# Revit family: xFaucet-Single_Control-American_Standard-Colony_Pro-7075.10x_Series
name_source: partatom
category: Plumbing Fixtures
revit_build: Autodesk Revit 2014 (Build: 20130308_1515(x64)
units: mm (PartAtom-declared; Revit-internal decimal feet)

## types (3) — shared parameters
ADA Compliant = Yes
Assembly Code = D2020300
CW Connection = Yes
CWFU = 1.5
Cold Water Connection Diameter = 3/8"
Cold Water Connection Radius = 3/16"
Default Elevation = 0"
Flow Rate = 1.2 gmp/4.5 L/min
HW Connection = Yes
HWFU = 1.5
Height = 6 3/16"
Hot Water Connection Diameter = 0"
Hot Water Connection Radius = 3/16"
Installation Type = Fitting can be mounted on 4" centers using optional escutcheon (2000.102P) or single hole mounting method.
Length = 6 3/8"
Manufacturer = American Standard
Material = Metal-American Standard-002-Polished Chrome
Price = Prices may vary. Please consult Manufacturer Representative for most up-to-date price list.
Product URL = https://www.americanstandard-us.com
URL = http://www.americanstandard-us.com
Vent Connection = No
Warranty Information = Faucet Lifetime Function And Finish Limited Warranty.
Waste Connection = No
Width = 2"
zero-valued in all types: WFU

## per-type parameters (varying)
| type | Description | Pop-up drain handle |
| 7075.100 | Colony PRO Single Control Lavatory Faucet. Metal lever handle. Metal pop-up drain. | Yes |
| 7075.102 | Colony PRO Single Control Lavatory Faucet. Metal lever handle. 50/50 pop-up drain. | Yes |
| 7075.104 | Colony PRO Single Control Lavatory Faucet.  Metal lever handle. LESS drain. LESS pop-up rod & hole. | No |

note: column(s) folded — value = type name in every type: Model

## geometry (parser evidence)
native form markers: Sweep x1
no freeform markers — native parametric forms only
